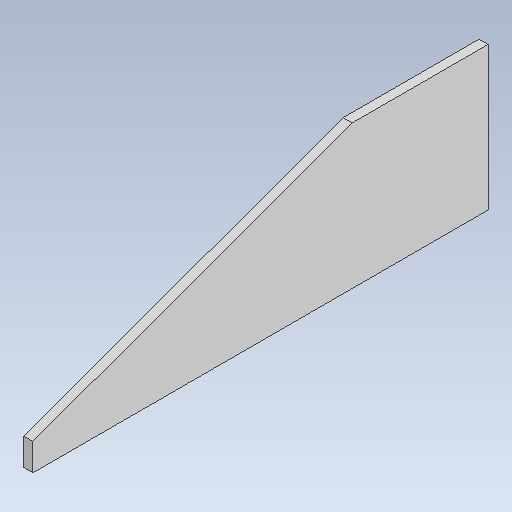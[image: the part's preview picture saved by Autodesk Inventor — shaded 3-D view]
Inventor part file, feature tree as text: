
AUTODESK INVENTOR PART (.ipt)
format: ipt  version: 2021 (Build 250183000, 183)  size: 95,744 bytes
history: native  units: in
note: dims shown in document units (in); Inventor stores cm internally (conversion verified against a paired STEP export)
features: extrude x1, sketch x1
ambient origin geometry x8: Origin, YZ Plane, XZ Plane, XY Plane, X Axis, Y Axis, Z Axis, Center Point
bodies: Solid1 (feature_tree)
feature tree (2):
  extrude  "Extrusion1"  Depth=0.1in TaperAngle=0.0deg
  sketch  "Sketch1"  dims[d1=3.75in d2=0.1in d3=0.0in d4=0.1374in d5=0.3in d6=1.5in]
